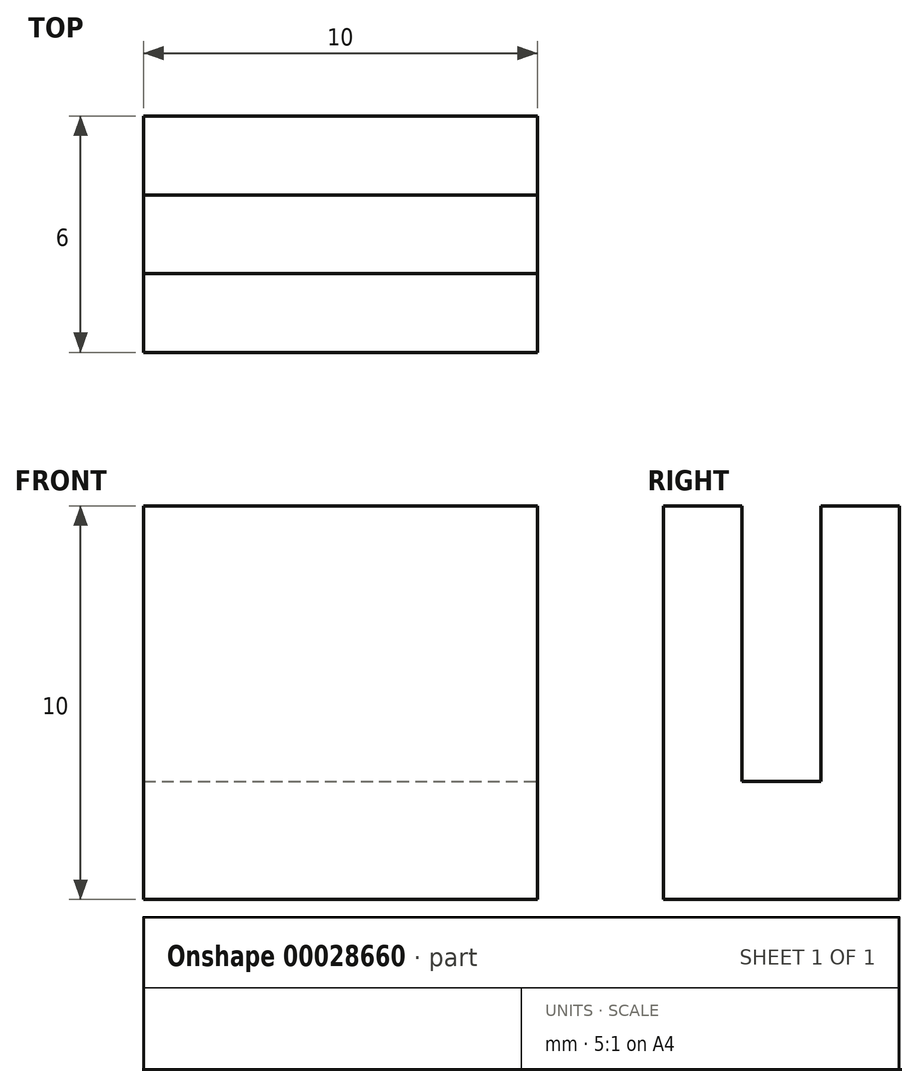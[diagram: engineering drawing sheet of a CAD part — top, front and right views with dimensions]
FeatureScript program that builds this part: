
annotation { "Feature Type Name" : "Feature", "Feature Type Description" : "" }
export const myFeature = defineFeature(function(context is Context, id is Id, definition is map)
    precondition{}
    {
        {
            var Q0;
            Q0=qCreatedBy(makeId("Top.planeOp"),FACE);
            var sketch = newSketch(context, id + "F0", { "sketchPlane" : qUnion([Q0])});
            skLineSegment(sketch, "E0.bottom", {"start": v(-25.19, 3) * mm, "end": v(-15.19, 3) * mm});
            skLineSegment(sketch, "E0.top", {"start": v(-25.19, -3) * mm, "end": v(-15.19, -3) * mm});
            skLineSegment(sketch, "E0.left", {"start": v(-25.19, 3) * mm, "end": v(-25.19, -3) * mm});
            skLineSegment(sketch, "E0.right", {"start": v(-15.19, 3) * mm, "end": v(-15.19, -3) * mm});
            skPoint(sketch, "E1", {"position": v(-25.19, 0) * mm});
            skLineSegment(sketch, "E2.bottom", {"start": v(-25.19, 1) * mm, "end": v(-15.19, 1) * mm, "construction": true});
            skLineSegment(sketch, "E2.top", {"start": v(-25.19, -1) * mm, "end": v(-15.19, -1) * mm, "construction": true});
            skLineSegment(sketch, "E2.left", {"start": v(-25.19, 1) * mm, "end": v(-25.19, -1) * mm, "construction": true});
            skLineSegment(sketch, "E2.right", {"start": v(-15.19, 1) * mm, "end": v(-15.19, -1) * mm, "construction": true});
            skSolve(sketch);
        }
        {
            var Q0;
            Q0=makeQuery(id+"F0.imprint","IMPRINT",FACE,{"disambiguationData":[TD([[makeQuery(id+"F0.imprint","IMPRINT",EDGE,{"derivedFrom":sQuery(id+"F0.wireOp",EDGE,"E0.bottom")}),-1.0]])]});
            extrude(context, id + "F1", {"entities" : qUnion([Q0]), "depth" : 10 * mm});
        }
        {
            var Q0;
            Q0=makeQuery(id+"F1.opExtrude","CAP_FACE",FACE,{"disambiguationData":[OSD([sQuery(id+"F0.wireOp",EDGE,"E0.bottom"),sQuery(id+"F0.wireOp",EDGE,"E0.top"),sQuery(id+"F0.wireOp",EDGE,"E0.left"),sQuery(id+"F0.wireOp",EDGE,"E0.right")])],"isStart":false});
            var sketch = newSketch(context, id + "F2", { "sketchPlane" : qUnion([Q0])});
            skLineSegment(sketch, "E3.bottom", {"start": v(-25.19, 1) * mm, "end": v(-15.19, 1) * mm});
            skLineSegment(sketch, "E3.top", {"start": v(-25.19, -1) * mm, "end": v(-15.19, -1) * mm});
            skLineSegment(sketch, "E3.left", {"start": v(-25.19, 1) * mm, "end": v(-25.19, -1) * mm});
            skLineSegment(sketch, "E3.right", {"start": v(-15.19, 1) * mm, "end": v(-15.19, -1) * mm});
            skSolve(sketch);
        }
        {
            var Q0;
            Q0 = qSketchRegion(id + "F2", true);
            extrude(context, id + "F3", {"entities" : qUnion([Q0]), "operationType" : NewBodyOperationType.REMOVE, "oppositeDirection" : true, "depth" : 7 * mm});
        }
    });
